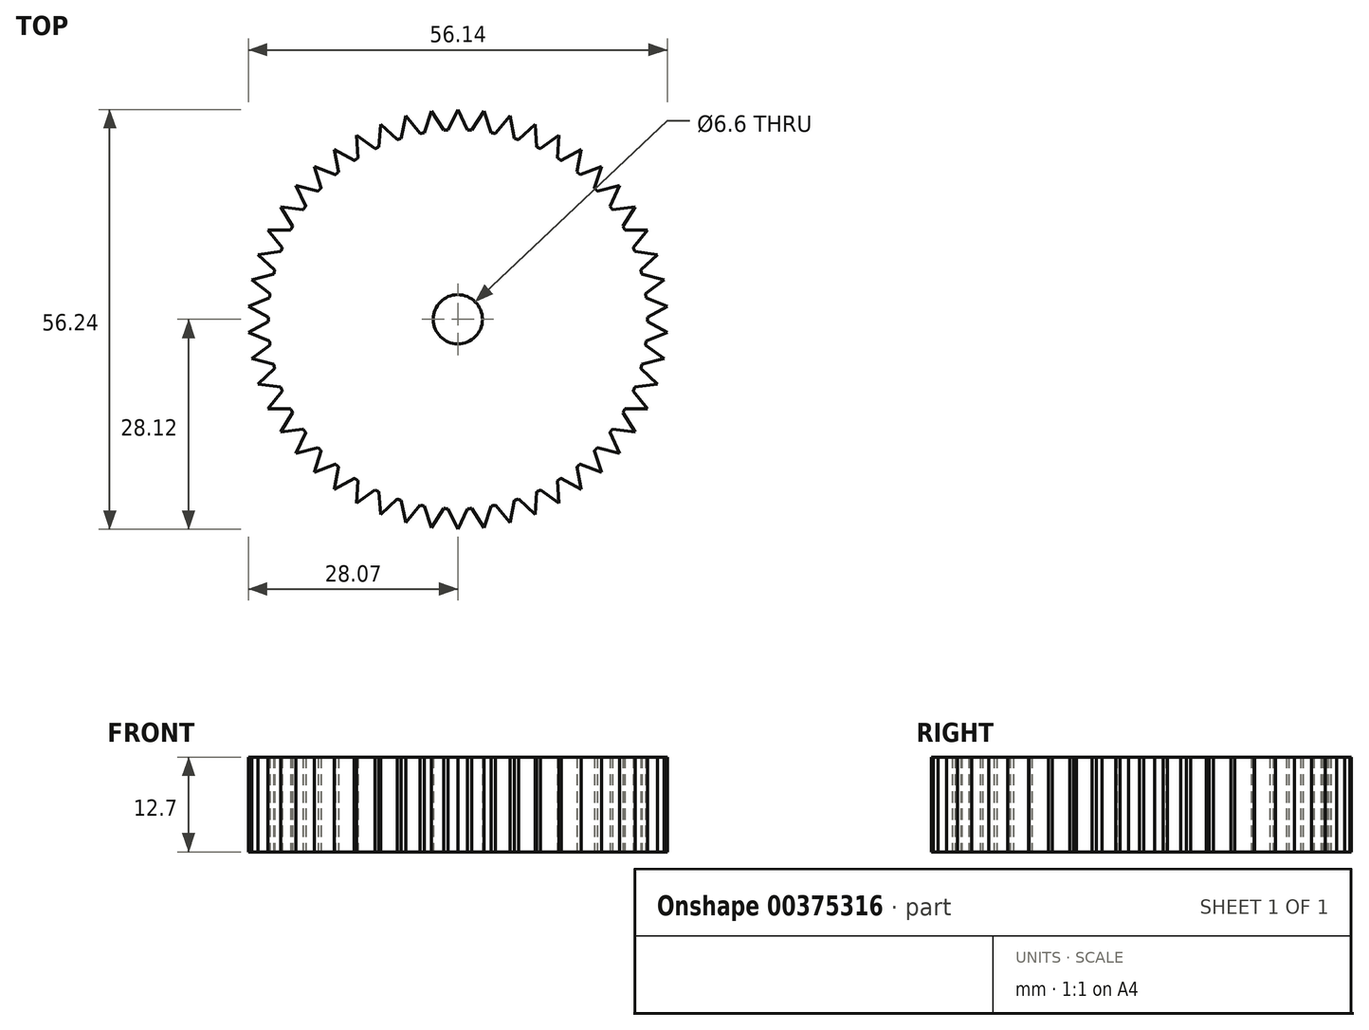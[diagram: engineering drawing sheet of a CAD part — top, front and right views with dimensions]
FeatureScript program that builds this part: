
annotation { "Feature Type Name" : "Feature", "Feature Type Description" : "" }
export const myFeature = defineFeature(function(context is Context, id is Id, definition is map)
    precondition{}
    {
        {
            var Q0;
            Q0=qCreatedBy(makeId("Top.planeOp"),FACE);
            var sketch = newSketch(context, id + "F0", { "sketchPlane" : qUnion([Q0])});
            skCircle(sketch, "E0", {"center": v(0, 0) * mm, "radius": 25.4 * mm});
            skCircle(sketch, "E1", {"center": v(0, 0) * mm, "radius": 3.3 * mm});
            skLineSegment(sketch, "E2", {"start": v(0, 28.12) * mm, "end": v(1.3, 25.37) * mm});
            skLineSegment(sketch, "E3", {"start": v(0, 28.12) * mm, "end": v(-1.3, 25.37) * mm});
            skLineSegment(sketch, "E4.1.0", {"start": v(-3.52, 27.9) * mm, "end": v(-4.47, 25) * mm});
            skLineSegment(sketch, "E4.1.1", {"start": v(-3.52, 27.9) * mm, "end": v(-1.89, 25.33) * mm});
            skLineSegment(sketch, "E4.2.0", {"start": v(-7, 27.24) * mm, "end": v(-7.57, 24.25) * mm});
            skLineSegment(sketch, "E4.2.1", {"start": v(-7, 27.24) * mm, "end": v(-5.05, 24.9) * mm});
            skLineSegment(sketch, "E4.3.0", {"start": v(-10.35, 26.15) * mm, "end": v(-10.55, 23.1) * mm});
            skLineSegment(sketch, "E4.3.1", {"start": v(-10.35, 26.15) * mm, "end": v(-8.13, 24.06) * mm});
            skLineSegment(sketch, "E4.4.0", {"start": v(-13.55, 24.64) * mm, "end": v(-13.36, 21.6) * mm});
            skLineSegment(sketch, "E4.4.1", {"start": v(-13.55, 24.64) * mm, "end": v(-11.08, 22.86) * mm});
            skLineSegment(sketch, "E4.5.0", {"start": v(-16.53, 22.75) * mm, "end": v(-15.96, 19.76) * mm});
            skLineSegment(sketch, "E4.5.1", {"start": v(-16.53, 22.75) * mm, "end": v(-13.86, 21.29) * mm});
            skLineSegment(sketch, "E4.6.0", {"start": v(-19.25, 20.5) * mm, "end": v(-18.31, 17.6) * mm});
            skLineSegment(sketch, "E4.6.1", {"start": v(-19.25, 20.5) * mm, "end": v(-16.41, 19.38) * mm});
            skLineSegment(sketch, "E4.7.0", {"start": v(-21.67, 17.93) * mm, "end": v(-20.38, 15.17) * mm});
            skLineSegment(sketch, "E4.7.1", {"start": v(-21.67, 17.93) * mm, "end": v(-18.71, 17.17) * mm});
            skLineSegment(sketch, "E4.8.0", {"start": v(-23.74, 15.07) * mm, "end": v(-22.12, 12.5) * mm});
            skLineSegment(sketch, "E4.8.1", {"start": v(-23.74, 15.07) * mm, "end": v(-20.72, 14.7) * mm});
            skLineSegment(sketch, "E4.9.0", {"start": v(-25.45, 11.97) * mm, "end": v(-23.5, 9.62) * mm});
            skLineSegment(sketch, "E4.9.1", {"start": v(-25.45, 11.97) * mm, "end": v(-22.4, 11.98) * mm});
            skLineSegment(sketch, "E4.10.0", {"start": v(-26.75, 8.7) * mm, "end": v(-24.53, 6.6) * mm});
            skLineSegment(sketch, "E4.10.1", {"start": v(-26.75, 8.7) * mm, "end": v(-23.72, 9.08) * mm});
            skLineSegment(sketch, "E4.11.0", {"start": v(-27.62, 5.27) * mm, "end": v(-25.16, 3.47) * mm});
            skLineSegment(sketch, "E4.11.1", {"start": v(-27.62, 5.27) * mm, "end": v(-24.67, 6.03) * mm});
            skLineSegment(sketch, "E4.12.0", {"start": v(-28.07, 1.77) * mm, "end": v(-25.4, 0.3) * mm});
            skLineSegment(sketch, "E4.12.1", {"start": v(-28.07, 1.77) * mm, "end": v(-25.23, 2.9) * mm});
            skLineSegment(sketch, "E4.13.0", {"start": v(-28.07, -1.77) * mm, "end": v(-25.23, -2.9) * mm});
            skLineSegment(sketch, "E4.13.1", {"start": v(-28.07, -1.77) * mm, "end": v(-25.4, -0.3) * mm});
            skLineSegment(sketch, "E4.14.0", {"start": v(-27.62, -5.27) * mm, "end": v(-24.67, -6.03) * mm});
            skLineSegment(sketch, "E4.14.1", {"start": v(-27.62, -5.27) * mm, "end": v(-25.16, -3.47) * mm});
            skLineSegment(sketch, "E4.15.0", {"start": v(-26.75, -8.7) * mm, "end": v(-23.72, -9.08) * mm});
            skLineSegment(sketch, "E4.15.1", {"start": v(-26.75, -8.7) * mm, "end": v(-24.53, -6.6) * mm});
            skLineSegment(sketch, "E4.16.0", {"start": v(-25.45, -11.97) * mm, "end": v(-22.4, -11.98) * mm});
            skLineSegment(sketch, "E4.16.1", {"start": v(-25.45, -11.97) * mm, "end": v(-23.5, -9.62) * mm});
            skLineSegment(sketch, "E4.17.0", {"start": v(-23.74, -15.07) * mm, "end": v(-20.72, -14.7) * mm});
            skLineSegment(sketch, "E4.17.1", {"start": v(-23.74, -15.07) * mm, "end": v(-22.12, -12.5) * mm});
            skLineSegment(sketch, "E4.18.0", {"start": v(-21.67, -17.93) * mm, "end": v(-18.71, -17.17) * mm});
            skLineSegment(sketch, "E4.18.1", {"start": v(-21.67, -17.93) * mm, "end": v(-20.38, -15.17) * mm});
            skLineSegment(sketch, "E4.19.0", {"start": v(-19.25, -20.5) * mm, "end": v(-16.41, -19.38) * mm});
            skLineSegment(sketch, "E4.19.1", {"start": v(-19.25, -20.5) * mm, "end": v(-18.31, -17.6) * mm});
            skLineSegment(sketch, "E4.20.0", {"start": v(-16.53, -22.75) * mm, "end": v(-13.86, -21.29) * mm});
            skLineSegment(sketch, "E4.20.1", {"start": v(-16.53, -22.75) * mm, "end": v(-15.96, -19.76) * mm});
            skLineSegment(sketch, "E4.21.0", {"start": v(-13.55, -24.64) * mm, "end": v(-11.08, -22.86) * mm});
            skLineSegment(sketch, "E4.21.1", {"start": v(-13.55, -24.64) * mm, "end": v(-13.36, -21.6) * mm});
            skLineSegment(sketch, "E4.22.0", {"start": v(-10.35, -26.15) * mm, "end": v(-8.13, -24.06) * mm});
            skLineSegment(sketch, "E4.22.1", {"start": v(-10.35, -26.15) * mm, "end": v(-10.55, -23.1) * mm});
            skLineSegment(sketch, "E4.23.0", {"start": v(-7, -27.24) * mm, "end": v(-5.05, -24.9) * mm});
            skLineSegment(sketch, "E4.23.1", {"start": v(-7, -27.24) * mm, "end": v(-7.57, -24.25) * mm});
            skLineSegment(sketch, "E4.24.0", {"start": v(-3.52, -27.9) * mm, "end": v(-1.89, -25.33) * mm});
            skLineSegment(sketch, "E4.24.1", {"start": v(-3.52, -27.9) * mm, "end": v(-4.47, -25) * mm});
            skLineSegment(sketch, "E4.25.0", {"start": v(0, -28.12) * mm, "end": v(1.3, -25.37) * mm});
            skLineSegment(sketch, "E4.25.1", {"start": v(0, -28.12) * mm, "end": v(-1.3, -25.37) * mm});
            skLineSegment(sketch, "E4.26.0", {"start": v(3.52, -27.9) * mm, "end": v(4.47, -25) * mm});
            skLineSegment(sketch, "E4.26.1", {"start": v(3.52, -27.9) * mm, "end": v(1.89, -25.33) * mm});
            skLineSegment(sketch, "E4.27.0", {"start": v(7, -27.24) * mm, "end": v(7.57, -24.25) * mm});
            skLineSegment(sketch, "E4.27.1", {"start": v(7, -27.24) * mm, "end": v(5.05, -24.9) * mm});
            skLineSegment(sketch, "E4.28.0", {"start": v(10.35, -26.15) * mm, "end": v(10.55, -23.1) * mm});
            skLineSegment(sketch, "E4.28.1", {"start": v(10.35, -26.15) * mm, "end": v(8.13, -24.06) * mm});
            skLineSegment(sketch, "E4.29.0", {"start": v(13.55, -24.64) * mm, "end": v(13.36, -21.6) * mm});
            skLineSegment(sketch, "E4.29.1", {"start": v(13.55, -24.64) * mm, "end": v(11.08, -22.86) * mm});
            skLineSegment(sketch, "E4.30.0", {"start": v(16.53, -22.75) * mm, "end": v(15.96, -19.76) * mm});
            skLineSegment(sketch, "E4.30.1", {"start": v(16.53, -22.75) * mm, "end": v(13.86, -21.29) * mm});
            skLineSegment(sketch, "E4.31.0", {"start": v(19.25, -20.5) * mm, "end": v(18.31, -17.6) * mm});
            skLineSegment(sketch, "E4.31.1", {"start": v(19.25, -20.5) * mm, "end": v(16.41, -19.38) * mm});
            skLineSegment(sketch, "E4.32.0", {"start": v(21.67, -17.93) * mm, "end": v(20.38, -15.17) * mm});
            skLineSegment(sketch, "E4.32.1", {"start": v(21.67, -17.93) * mm, "end": v(18.71, -17.17) * mm});
            skLineSegment(sketch, "E4.33.0", {"start": v(23.74, -15.07) * mm, "end": v(22.12, -12.5) * mm});
            skLineSegment(sketch, "E4.33.1", {"start": v(23.74, -15.07) * mm, "end": v(20.72, -14.7) * mm});
            skLineSegment(sketch, "E4.34.0", {"start": v(25.45, -11.97) * mm, "end": v(23.5, -9.62) * mm});
            skLineSegment(sketch, "E4.34.1", {"start": v(25.45, -11.97) * mm, "end": v(22.4, -11.98) * mm});
            skLineSegment(sketch, "E4.35.0", {"start": v(26.75, -8.7) * mm, "end": v(24.53, -6.6) * mm});
            skLineSegment(sketch, "E4.35.1", {"start": v(26.75, -8.7) * mm, "end": v(23.72, -9.08) * mm});
            skLineSegment(sketch, "E4.36.0", {"start": v(27.62, -5.27) * mm, "end": v(25.16, -3.47) * mm});
            skLineSegment(sketch, "E4.36.1", {"start": v(27.62, -5.27) * mm, "end": v(24.67, -6.03) * mm});
            skLineSegment(sketch, "E4.37.0", {"start": v(28.07, -1.77) * mm, "end": v(25.4, -0.3) * mm});
            skLineSegment(sketch, "E4.37.1", {"start": v(28.07, -1.77) * mm, "end": v(25.23, -2.9) * mm});
            skLineSegment(sketch, "E4.38.0", {"start": v(28.07, 1.77) * mm, "end": v(25.23, 2.9) * mm});
            skLineSegment(sketch, "E4.38.1", {"start": v(28.07, 1.77) * mm, "end": v(25.4, 0.3) * mm});
            skLineSegment(sketch, "E4.39.0", {"start": v(27.62, 5.27) * mm, "end": v(24.67, 6.03) * mm});
            skLineSegment(sketch, "E4.39.1", {"start": v(27.62, 5.27) * mm, "end": v(25.16, 3.47) * mm});
            skLineSegment(sketch, "E4.40.0", {"start": v(26.75, 8.7) * mm, "end": v(23.72, 9.08) * mm});
            skLineSegment(sketch, "E4.40.1", {"start": v(26.75, 8.7) * mm, "end": v(24.53, 6.6) * mm});
            skLineSegment(sketch, "E4.41.0", {"start": v(25.45, 11.97) * mm, "end": v(22.4, 11.98) * mm});
            skLineSegment(sketch, "E4.41.1", {"start": v(25.45, 11.97) * mm, "end": v(23.5, 9.62) * mm});
            skLineSegment(sketch, "E4.42.0", {"start": v(23.74, 15.07) * mm, "end": v(20.72, 14.7) * mm});
            skLineSegment(sketch, "E4.42.1", {"start": v(23.74, 15.07) * mm, "end": v(22.12, 12.5) * mm});
            skLineSegment(sketch, "E4.43.0", {"start": v(21.67, 17.93) * mm, "end": v(18.71, 17.17) * mm});
            skLineSegment(sketch, "E4.43.1", {"start": v(21.67, 17.93) * mm, "end": v(20.38, 15.17) * mm});
            skLineSegment(sketch, "E4.44.0", {"start": v(19.25, 20.5) * mm, "end": v(16.41, 19.38) * mm});
            skLineSegment(sketch, "E4.44.1", {"start": v(19.25, 20.5) * mm, "end": v(18.31, 17.6) * mm});
            skLineSegment(sketch, "E4.45.0", {"start": v(16.53, 22.75) * mm, "end": v(13.86, 21.29) * mm});
            skLineSegment(sketch, "E4.45.1", {"start": v(16.53, 22.75) * mm, "end": v(15.96, 19.76) * mm});
            skLineSegment(sketch, "E4.46.0", {"start": v(13.55, 24.64) * mm, "end": v(11.08, 22.86) * mm});
            skLineSegment(sketch, "E4.46.1", {"start": v(13.55, 24.64) * mm, "end": v(13.36, 21.6) * mm});
            skLineSegment(sketch, "E4.47.0", {"start": v(10.35, 26.15) * mm, "end": v(8.13, 24.06) * mm});
            skLineSegment(sketch, "E4.47.1", {"start": v(10.35, 26.15) * mm, "end": v(10.55, 23.1) * mm});
            skLineSegment(sketch, "E4.48.0", {"start": v(7, 27.24) * mm, "end": v(5.05, 24.9) * mm});
            skLineSegment(sketch, "E4.48.1", {"start": v(7, 27.24) * mm, "end": v(7.57, 24.25) * mm});
            skLineSegment(sketch, "E4.49.0", {"start": v(3.52, 27.9) * mm, "end": v(1.89, 25.33) * mm});
            skLineSegment(sketch, "E4.49.1", {"start": v(3.52, 27.9) * mm, "end": v(4.47, 25) * mm});
            skSolve(sketch);
        }
        {
            var Q0;
            {var subQ0=sQuery(id+"F0.wireOp",EDGE,"E4.33.0");Q0=makeQuery(id+"F0.imprint","IMPRINT",FACE,{"disambiguationData":[TD([[makeQuery(id+"F0.imprint","IMPRINT",EDGE,{"derivedFrom":subQ0}),1.0]])]});}
            var Q1;
            {var subQ0=sQuery(id+"F0.wireOp",EDGE,"E4.31.0");Q1=makeQuery(id+"F0.imprint","IMPRINT",FACE,{"disambiguationData":[TD([[makeQuery(id+"F0.imprint","IMPRINT",EDGE,{"derivedFrom":subQ0}),1.0]])]});}
            var Q2;
            {var subQ0=sQuery(id+"F0.wireOp",EDGE,"E4.15.0");Q2=makeQuery(id+"F0.imprint","IMPRINT",FACE,{"disambiguationData":[TD([[makeQuery(id+"F0.imprint","IMPRINT",EDGE,{"derivedFrom":subQ0}),1.0]])]});}
            var Q3;
            {var subQ0=sQuery(id+"F0.wireOp",EDGE,"E4.32.0");Q3=makeQuery(id+"F0.imprint","IMPRINT",FACE,{"disambiguationData":[TD([[makeQuery(id+"F0.imprint","IMPRINT",EDGE,{"derivedFrom":subQ0}),1.0]])]});}
            var Q4;
            {var subQ0=sQuery(id+"F0.wireOp",EDGE,"E4.16.0");Q4=makeQuery(id+"F0.imprint","IMPRINT",FACE,{"disambiguationData":[TD([[makeQuery(id+"F0.imprint","IMPRINT",EDGE,{"derivedFrom":subQ0}),1.0]])]});}
            var Q5;
            {var subQ0=sQuery(id+"F0.wireOp",EDGE,"E4.5.0");Q5=makeQuery(id+"F0.imprint","IMPRINT",FACE,{"disambiguationData":[TD([[makeQuery(id+"F0.imprint","IMPRINT",EDGE,{"derivedFrom":subQ0}),1.0]])]});}
            var Q6;
            {var subQ0=sQuery(id+"F0.wireOp",EDGE,"E4.21.0");Q6=makeQuery(id+"F0.imprint","IMPRINT",FACE,{"disambiguationData":[TD([[makeQuery(id+"F0.imprint","IMPRINT",EDGE,{"derivedFrom":subQ0}),1.0]])]});}
            var Q7;
            Q7=makeQuery(id+"F0.imprint","IMPRINT",FACE,{"disambiguationData":[TD([[makeQuery(id+"F0.imprint","IMPRINT",EDGE,{"derivedFrom":sQuery(id+"F0.wireOp",EDGE,"E1")}),-1.0]])]});
            var Q8;
            {var subQ0=sQuery(id+"F0.wireOp",EDGE,"E4.23.0");Q8=makeQuery(id+"F0.imprint","IMPRINT",FACE,{"disambiguationData":[TD([[makeQuery(id+"F0.imprint","IMPRINT",EDGE,{"derivedFrom":subQ0}),1.0]])]});}
            var Q9;
            {var subQ0=sQuery(id+"F0.wireOp",EDGE,"E4.24.0");Q9=makeQuery(id+"F0.imprint","IMPRINT",FACE,{"disambiguationData":[TD([[makeQuery(id+"F0.imprint","IMPRINT",EDGE,{"derivedFrom":subQ0}),1.0]])]});}
            var Q10;
            {var subQ0=sQuery(id+"F0.wireOp",EDGE,"E4.9.0");Q10=makeQuery(id+"F0.imprint","IMPRINT",FACE,{"disambiguationData":[TD([[makeQuery(id+"F0.imprint","IMPRINT",EDGE,{"derivedFrom":subQ0}),1.0]])]});}
            var Q11;
            {var subQ0=sQuery(id+"F0.wireOp",EDGE,"E4.26.0");Q11=makeQuery(id+"F0.imprint","IMPRINT",FACE,{"disambiguationData":[TD([[makeQuery(id+"F0.imprint","IMPRINT",EDGE,{"derivedFrom":subQ0}),1.0]])]});}
            var Q12;
            {var subQ0=sQuery(id+"F0.wireOp",EDGE,"E4.10.0");Q12=makeQuery(id+"F0.imprint","IMPRINT",FACE,{"disambiguationData":[TD([[makeQuery(id+"F0.imprint","IMPRINT",EDGE,{"derivedFrom":subQ0}),1.0]])]});}
            var Q13;
            {var subQ0=sQuery(id+"F0.wireOp",EDGE,"E4.3.0");Q13=makeQuery(id+"F0.imprint","IMPRINT",FACE,{"disambiguationData":[TD([[makeQuery(id+"F0.imprint","IMPRINT",EDGE,{"derivedFrom":subQ0}),1.0]])]});}
            var Q14;
            {var subQ0=sQuery(id+"F0.wireOp",EDGE,"E4.42.0");Q14=makeQuery(id+"F0.imprint","IMPRINT",FACE,{"disambiguationData":[TD([[makeQuery(id+"F0.imprint","IMPRINT",EDGE,{"derivedFrom":subQ0}),1.0]])]});}
            var Q15;
            {var subQ0=sQuery(id+"F0.wireOp",EDGE,"E4.43.0");Q15=makeQuery(id+"F0.imprint","IMPRINT",FACE,{"disambiguationData":[TD([[makeQuery(id+"F0.imprint","IMPRINT",EDGE,{"derivedFrom":subQ0}),1.0]])]});}
            var Q16;
            {var subQ0=sQuery(id+"F0.wireOp",EDGE,"E4.45.0");Q16=makeQuery(id+"F0.imprint","IMPRINT",FACE,{"disambiguationData":[TD([[makeQuery(id+"F0.imprint","IMPRINT",EDGE,{"derivedFrom":subQ0}),1.0]])]});}
            var Q17;
            {var subQ0=sQuery(id+"F0.wireOp",EDGE,"E4.47.0");Q17=makeQuery(id+"F0.imprint","IMPRINT",FACE,{"disambiguationData":[TD([[makeQuery(id+"F0.imprint","IMPRINT",EDGE,{"derivedFrom":subQ0}),1.0]])]});}
            var Q18;
            {var subQ0=sQuery(id+"F0.wireOp",EDGE,"E4.27.0");Q18=makeQuery(id+"F0.imprint","IMPRINT",FACE,{"disambiguationData":[TD([[makeQuery(id+"F0.imprint","IMPRINT",EDGE,{"derivedFrom":subQ0}),1.0]])]});}
            var Q19;
            {var subQ0=sQuery(id+"F0.wireOp",EDGE,"E4.19.0");Q19=makeQuery(id+"F0.imprint","IMPRINT",FACE,{"disambiguationData":[TD([[makeQuery(id+"F0.imprint","IMPRINT",EDGE,{"derivedFrom":subQ0}),1.0]])]});}
            var Q20;
            {var subQ0=sQuery(id+"F0.wireOp",EDGE,"E4.29.0");Q20=makeQuery(id+"F0.imprint","IMPRINT",FACE,{"disambiguationData":[TD([[makeQuery(id+"F0.imprint","IMPRINT",EDGE,{"derivedFrom":subQ0}),1.0]])]});}
            var Q21;
            {var subQ0=sQuery(id+"F0.wireOp",EDGE,"E4.30.0");Q21=makeQuery(id+"F0.imprint","IMPRINT",FACE,{"disambiguationData":[TD([[makeQuery(id+"F0.imprint","IMPRINT",EDGE,{"derivedFrom":subQ0}),1.0]])]});}
            var Q22;
            {var subQ0=sQuery(id+"F0.wireOp",EDGE,"E4.14.0");Q22=makeQuery(id+"F0.imprint","IMPRINT",FACE,{"disambiguationData":[TD([[makeQuery(id+"F0.imprint","IMPRINT",EDGE,{"derivedFrom":subQ0}),1.0]])]});}
            var Q23;
            {var subQ0=sQuery(id+"F0.wireOp",EDGE,"E4.17.0");Q23=makeQuery(id+"F0.imprint","IMPRINT",FACE,{"disambiguationData":[TD([[makeQuery(id+"F0.imprint","IMPRINT",EDGE,{"derivedFrom":subQ0}),1.0]])]});}
            var Q24;
            {var subQ0=sQuery(id+"F0.wireOp",EDGE,"E4.34.0");Q24=makeQuery(id+"F0.imprint","IMPRINT",FACE,{"disambiguationData":[TD([[makeQuery(id+"F0.imprint","IMPRINT",EDGE,{"derivedFrom":subQ0}),1.0]])]});}
            var Q25;
            {var subQ0=sQuery(id+"F0.wireOp",EDGE,"E4.18.0");Q25=makeQuery(id+"F0.imprint","IMPRINT",FACE,{"disambiguationData":[TD([[makeQuery(id+"F0.imprint","IMPRINT",EDGE,{"derivedFrom":subQ0}),1.0]])]});}
            var Q26;
            {var subQ0=sQuery(id+"F0.wireOp",EDGE,"E4.4.0");Q26=makeQuery(id+"F0.imprint","IMPRINT",FACE,{"disambiguationData":[TD([[makeQuery(id+"F0.imprint","IMPRINT",EDGE,{"derivedFrom":subQ0}),1.0]])]});}
            var Q27;
            {var subQ0=sQuery(id+"F0.wireOp",EDGE,"E4.36.0");Q27=makeQuery(id+"F0.imprint","IMPRINT",FACE,{"disambiguationData":[TD([[makeQuery(id+"F0.imprint","IMPRINT",EDGE,{"derivedFrom":subQ0}),1.0]])]});}
            var Q28;
            {var subQ0=sQuery(id+"F0.wireOp",EDGE,"E4.20.0");Q28=makeQuery(id+"F0.imprint","IMPRINT",FACE,{"disambiguationData":[TD([[makeQuery(id+"F0.imprint","IMPRINT",EDGE,{"derivedFrom":subQ0}),1.0]])]});}
            var Q29;
            {var subQ0=sQuery(id+"F0.wireOp",EDGE,"E4.37.0");Q29=makeQuery(id+"F0.imprint","IMPRINT",FACE,{"disambiguationData":[TD([[makeQuery(id+"F0.imprint","IMPRINT",EDGE,{"derivedFrom":subQ0}),1.0]])]});}
            var Q30;
            {var subQ0=sQuery(id+"F0.wireOp",EDGE,"E4.6.0");Q30=makeQuery(id+"F0.imprint","IMPRINT",FACE,{"disambiguationData":[TD([[makeQuery(id+"F0.imprint","IMPRINT",EDGE,{"derivedFrom":subQ0}),1.0]])]});}
            var Q31;
            {var subQ0=sQuery(id+"F0.wireOp",EDGE,"E4.22.0");Q31=makeQuery(id+"F0.imprint","IMPRINT",FACE,{"disambiguationData":[TD([[makeQuery(id+"F0.imprint","IMPRINT",EDGE,{"derivedFrom":subQ0}),1.0]])]});}
            var Q32;
            {var subQ0=sQuery(id+"F0.wireOp",EDGE,"E4.7.0");Q32=makeQuery(id+"F0.imprint","IMPRINT",FACE,{"disambiguationData":[TD([[makeQuery(id+"F0.imprint","IMPRINT",EDGE,{"derivedFrom":subQ0}),1.0]])]});}
            var Q33;
            {var subQ0=sQuery(id+"F0.wireOp",EDGE,"E4.8.0");Q33=makeQuery(id+"F0.imprint","IMPRINT",FACE,{"disambiguationData":[TD([[makeQuery(id+"F0.imprint","IMPRINT",EDGE,{"derivedFrom":subQ0}),1.0]])]});}
            var Q34;
            {var subQ0=sQuery(id+"F0.wireOp",EDGE,"E4.25.0");Q34=makeQuery(id+"F0.imprint","IMPRINT",FACE,{"disambiguationData":[TD([[makeQuery(id+"F0.imprint","IMPRINT",EDGE,{"derivedFrom":subQ0}),1.0]])]});}
            var Q35;
            {var subQ0=sQuery(id+"F0.wireOp",EDGE,"E4.1.0");Q35=makeQuery(id+"F0.imprint","IMPRINT",FACE,{"disambiguationData":[TD([[makeQuery(id+"F0.imprint","IMPRINT",EDGE,{"derivedFrom":subQ0}),1.0]])]});}
            var Q36;
            {var subQ0=sQuery(id+"F0.wireOp",EDGE,"E4.2.0");Q36=makeQuery(id+"F0.imprint","IMPRINT",FACE,{"disambiguationData":[TD([[makeQuery(id+"F0.imprint","IMPRINT",EDGE,{"derivedFrom":subQ0}),1.0]])]});}
            var Q37;
            {var subQ0=sQuery(id+"F0.wireOp",EDGE,"E4.38.0");Q37=makeQuery(id+"F0.imprint","IMPRINT",FACE,{"disambiguationData":[TD([[makeQuery(id+"F0.imprint","IMPRINT",EDGE,{"derivedFrom":subQ0}),1.0]])]});}
            var Q38;
            {var subQ0=sQuery(id+"F0.wireOp",EDGE,"E4.39.0");Q38=makeQuery(id+"F0.imprint","IMPRINT",FACE,{"disambiguationData":[TD([[makeQuery(id+"F0.imprint","IMPRINT",EDGE,{"derivedFrom":subQ0}),1.0]])]});}
            var Q39;
            {var subQ0=sQuery(id+"F0.wireOp",EDGE,"E4.40.0");Q39=makeQuery(id+"F0.imprint","IMPRINT",FACE,{"disambiguationData":[TD([[makeQuery(id+"F0.imprint","IMPRINT",EDGE,{"derivedFrom":subQ0}),1.0]])]});}
            var Q40;
            {var subQ0=sQuery(id+"F0.wireOp",EDGE,"E4.41.0");Q40=makeQuery(id+"F0.imprint","IMPRINT",FACE,{"disambiguationData":[TD([[makeQuery(id+"F0.imprint","IMPRINT",EDGE,{"derivedFrom":subQ0}),1.0]])]});}
            var Q41;
            {var subQ0=sQuery(id+"F0.wireOp",EDGE,"E4.44.0");Q41=makeQuery(id+"F0.imprint","IMPRINT",FACE,{"disambiguationData":[TD([[makeQuery(id+"F0.imprint","IMPRINT",EDGE,{"derivedFrom":subQ0}),1.0]])]});}
            var Q42;
            {var subQ0=sQuery(id+"F0.wireOp",EDGE,"E4.46.0");Q42=makeQuery(id+"F0.imprint","IMPRINT",FACE,{"disambiguationData":[TD([[makeQuery(id+"F0.imprint","IMPRINT",EDGE,{"derivedFrom":subQ0}),1.0]])]});}
            var Q43;
            {var subQ0=sQuery(id+"F0.wireOp",EDGE,"E4.48.0");Q43=makeQuery(id+"F0.imprint","IMPRINT",FACE,{"disambiguationData":[TD([[makeQuery(id+"F0.imprint","IMPRINT",EDGE,{"derivedFrom":subQ0}),1.0]])]});}
            var Q44;
            {var subQ0=sQuery(id+"F0.wireOp",EDGE,"E4.49.0");Q44=makeQuery(id+"F0.imprint","IMPRINT",FACE,{"disambiguationData":[TD([[makeQuery(id+"F0.imprint","IMPRINT",EDGE,{"derivedFrom":subQ0}),1.0]])]});}
            var Q45;
            {var subQ0=sQuery(id+"F0.wireOp",EDGE,"E2");Q45=makeQuery(id+"F0.imprint","IMPRINT",FACE,{"disambiguationData":[TD([[makeQuery(id+"F0.imprint","IMPRINT",EDGE,{"derivedFrom":subQ0}),-1.0]])]});}
            var Q46;
            {var subQ0=sQuery(id+"F0.wireOp",EDGE,"E4.11.0");Q46=makeQuery(id+"F0.imprint","IMPRINT",FACE,{"disambiguationData":[TD([[makeQuery(id+"F0.imprint","IMPRINT",EDGE,{"derivedFrom":subQ0}),1.0]])]});}
            var Q47;
            {var subQ0=sQuery(id+"F0.wireOp",EDGE,"E4.28.0");Q47=makeQuery(id+"F0.imprint","IMPRINT",FACE,{"disambiguationData":[TD([[makeQuery(id+"F0.imprint","IMPRINT",EDGE,{"derivedFrom":subQ0}),1.0]])]});}
            var Q48;
            {var subQ0=sQuery(id+"F0.wireOp",EDGE,"E4.12.0");Q48=makeQuery(id+"F0.imprint","IMPRINT",FACE,{"disambiguationData":[TD([[makeQuery(id+"F0.imprint","IMPRINT",EDGE,{"derivedFrom":subQ0}),1.0]])]});}
            var Q49;
            {var subQ0=sQuery(id+"F0.wireOp",EDGE,"E4.13.0");Q49=makeQuery(id+"F0.imprint","IMPRINT",FACE,{"disambiguationData":[TD([[makeQuery(id+"F0.imprint","IMPRINT",EDGE,{"derivedFrom":subQ0}),1.0]])]});}
            var Q50;
            {var subQ0=sQuery(id+"F0.wireOp",EDGE,"E4.35.0");Q50=makeQuery(id+"F0.imprint","IMPRINT",FACE,{"disambiguationData":[TD([[makeQuery(id+"F0.imprint","IMPRINT",EDGE,{"derivedFrom":subQ0}),1.0]])]});}
            extrude(context, id + "F1", {"entities" : qUnion([Q0, Q1, Q2, Q3, Q4, Q5, Q6, Q7, Q8, Q9, Q10, Q11, Q12, Q13, Q14, Q15, Q16, Q17, Q18, Q19, Q20, Q21, Q22, Q23, Q24, Q25, Q26, Q27, Q28, Q29, Q30, Q31, Q32, Q33, Q34, Q35, Q36, Q37, Q38, Q39, Q40, Q41, Q42, Q43, Q44, Q45, Q46, Q47, Q48, Q49, Q50]), "depth" : 12.7 * mm});
        }
    });
